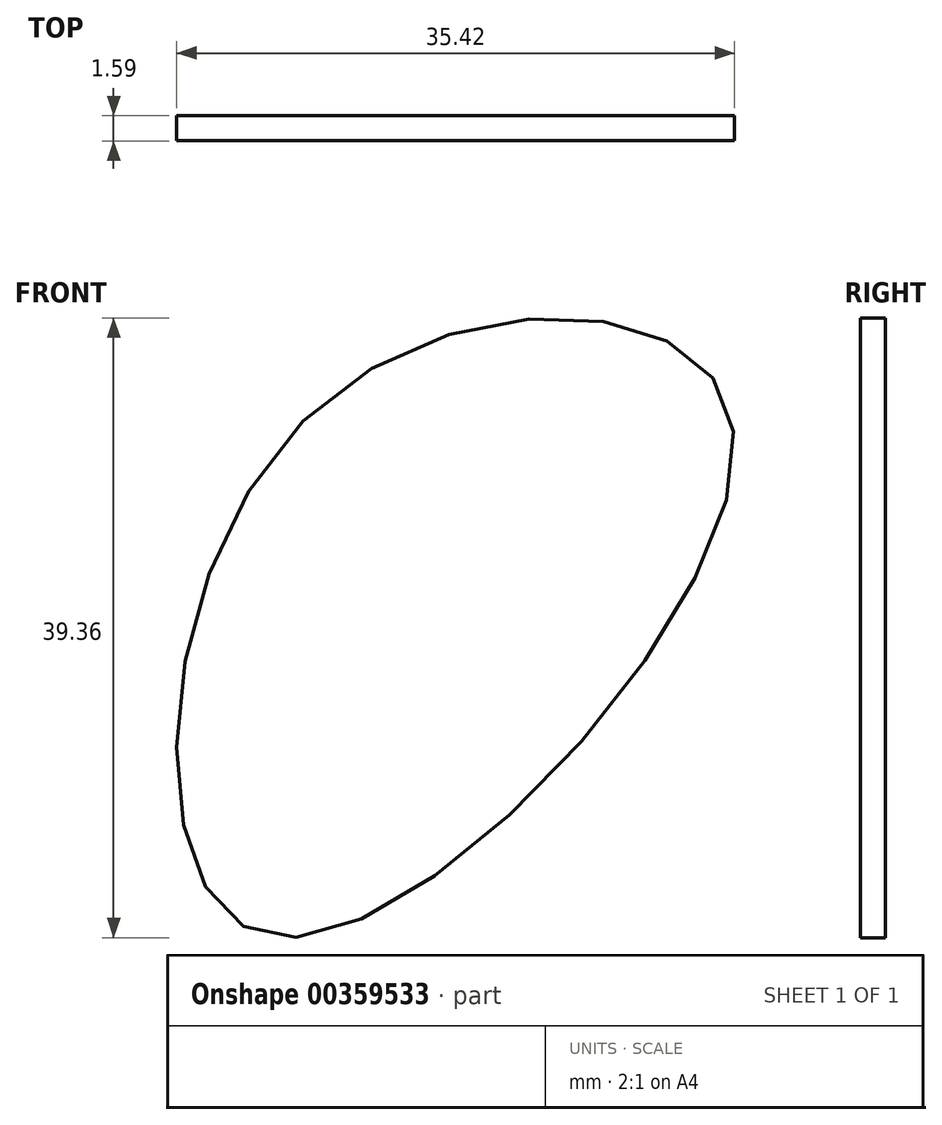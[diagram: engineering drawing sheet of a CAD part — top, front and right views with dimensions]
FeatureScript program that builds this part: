
annotation { "Feature Type Name" : "Feature", "Feature Type Description" : "" }
export const myFeature = defineFeature(function(context is Context, id is Id, definition is map)
    precondition{}
    {
        {
            var Q0;
            Q0=qCreatedBy(makeId("Front.planeOp"),FACE);
            var sketch = newSketch(context, id + "F0", { "sketchPlane" : qUnion([Q0])});
            skFitSpline(sketch, "E0", {"points": [v(-13.22, 0) * mm, v(14.04, 0) * mm, v(-15.48, -32.68) * mm, v(-13.22, 0) * mm]});
            skSolve(sketch);
        }
        {
            var Q0;
            Q0 = qSketchRegion(id + "F0", true);
            extrude(context, id + "F1", {"entities" : qUnion([Q0]), "depth" : 1.59 * mm});
        }
    });
